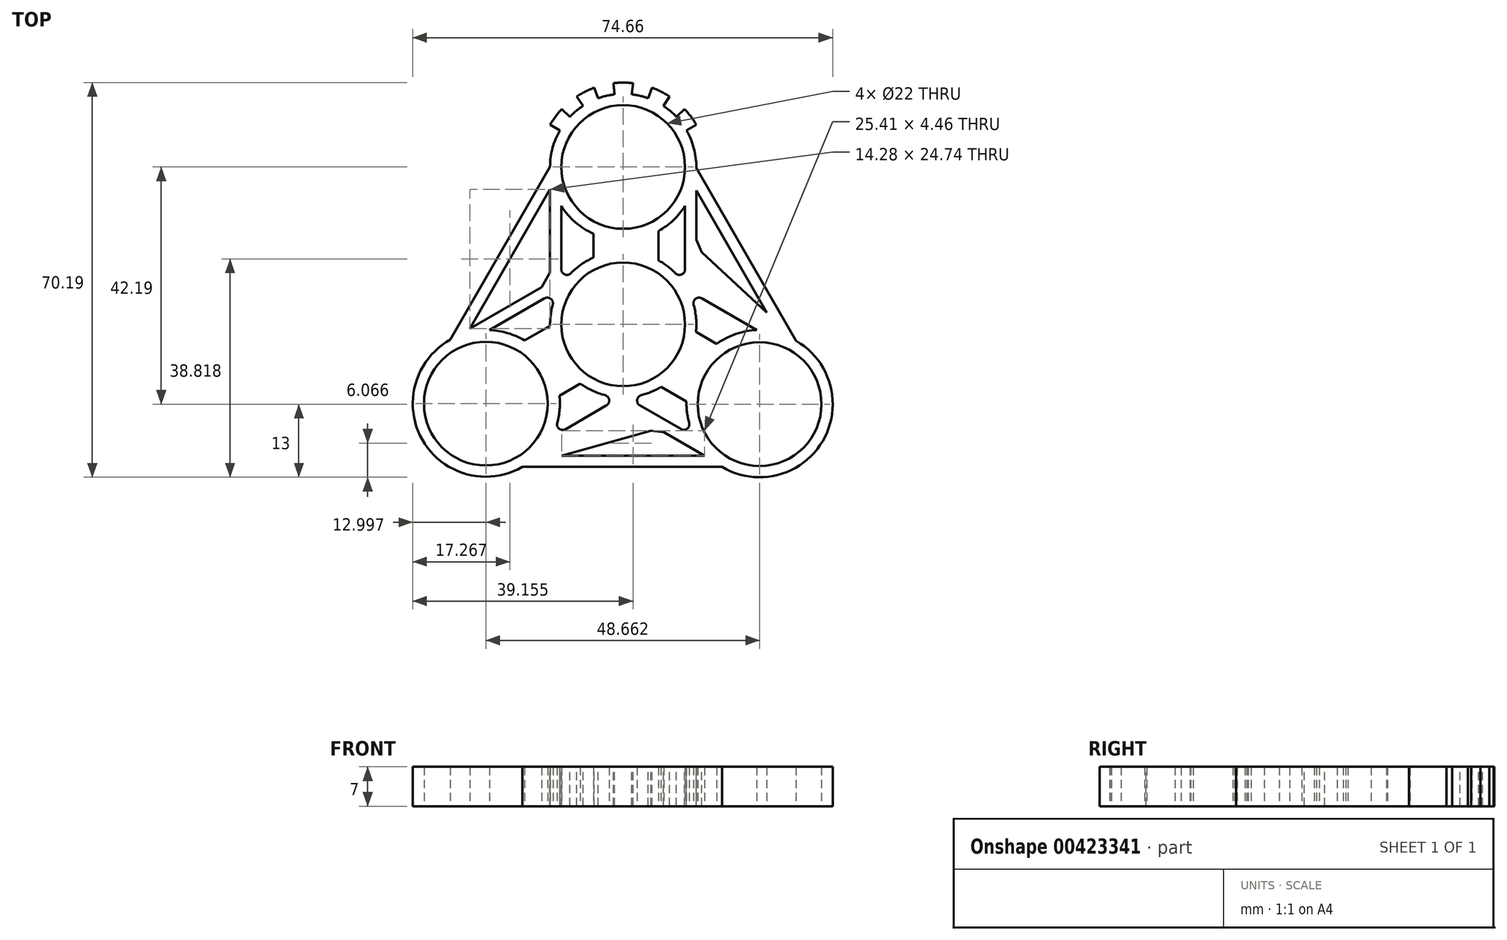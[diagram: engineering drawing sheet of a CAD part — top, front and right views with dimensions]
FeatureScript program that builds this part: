
annotation { "Feature Type Name" : "Feature", "Feature Type Description" : "" }
export const myFeature = defineFeature(function(context is Context, id is Id, definition is map)
    precondition{}
    {
        {
            var Q0;
            Q0=qCreatedBy(makeId("Top.planeOp"),FACE);
            var sketch = newSketch(context, id + "F0", { "sketchPlane" : qUnion([Q0])});
            skCircle(sketch, "E0", {"center": v(0, 0) * mm, "radius": 11 * mm});
            skCircle(sketch, "E1", {"center": v(0, 28) * mm, "radius": 11 * mm});
            skLineSegment(sketch, "E2", {"start": v(-11, 6.93) * mm, "end": v(-11, 21.07) * mm});
            skLineSegment(sketch, "E3", {"start": v(11, 21.07) * mm, "end": v(11, 6.93) * mm});
            skArc(sketch, "E4.0", {"start": v(-5.3, 11.87) * mm, "mid": v(-8.52, 9.82) * mm, "end": v(-11, 6.93) * mm});
            skArc(sketch, "E5.0", {"start": v(6.27, 16.61) * mm, "mid": v(8.92, 18.54) * mm, "end": v(11, 21.07) * mm});
            skLineSegment(sketch, "E6", {"start": v(-5.3, 11.87) * mm, "end": v(-5.3, 16.13) * mm});
            skLineSegment(sketch, "E7", {"start": v(6.27, 11.39) * mm, "end": v(6.27, 16.61) * mm});
            skPoint(sketch, "E8.orphan", {"position": v(-11, 0) * mm});
            skPoint(sketch, "E9.orphan", {"position": v(11, 0) * mm});
            skLineSegment(sketch, "E10.0", {"start": v(13, 23.81) * mm, "end": v(13, 13.72) * mm});
            skArc(sketch, "E11.trimOffspring", {"start": v(13, 27.81) * mm, "mid": v(0.1, 41) * mm, "end": v(-13, 28) * mm});
            skArc(sketch, "E12.trimOffspring", {"start": v(11, 6.93) * mm, "mid": v(8.92, 9.46) * mm, "end": v(6.27, 11.39) * mm});
            skArc(sketch, "E13.trimOffspring", {"start": v(-13, 0) * mm, "mid": v(-13, -0.13) * mm, "end": v(-13, -0.26) * mm});
            skArc(sketch, "E14.trimOffspring", {"start": v(-11, 21.07) * mm, "mid": v(-8.52, 18.18) * mm, "end": v(-5.3, 16.13) * mm});
            skArc(sketch, "E15.1.0", {"start": v(-30.75, -2.74) * mm, "mid": v(-35.72, -20.51) * mm, "end": v(-17.91, -25.35) * mm});
            skCircle(sketch, "E15.1.1", {"center": v(-24.41, -14.1) * mm, "radius": 11 * mm});
            skArc(sketch, "E15.2.0", {"start": v(17.59, -25.35) * mm, "mid": v(35.46, -20.77) * mm, "end": v(30.75, -2.93) * mm});
            skCircle(sketch, "E15.2.1", {"center": v(24.25, -14.19) * mm, "radius": 11 * mm});
            skPoint(sketch, "E15.center", {"position": v(-0.05, -0.1) * mm});
            skLineSegment(sketch, "E16.1.0", {"start": v(-27.29, -0.74) * mm, "end": v(-13, 7.5) * mm});
            skArc(sketch, "E16.1.1", {"start": v(-12.75, -20.06) * mm, "mid": v(-11.49, -16.47) * mm, "end": v(-11.32, -12.66) * mm});
            skLineSegment(sketch, "E16.1.2", {"start": v(-13, -0.26) * mm, "end": v(-17.52, -2.88) * mm});
            skArc(sketch, "E16.1.3", {"start": v(-11.5, 6.06) * mm, "mid": v(-12.65, 3) * mm, "end": v(-13, -0.26) * mm});
            skArc(sketch, "E16.1.5", {"start": v(-17.52, -2.88) * mm, "mid": v(-20.52, -1.55) * mm, "end": v(-23.75, -1) * mm});
            skLineSegment(sketch, "E16.1.6", {"start": v(-23.75, -1) * mm, "end": v(-11.5, 6.06) * mm});
            skLineSegment(sketch, "E16.2.0", {"start": v(14.45, -23.35) * mm, "end": v(6.14, -18.55) * mm});
            skArc(sketch, "E16.2.1", {"start": v(23.75, -1) * mm, "mid": v(20, -1.71) * mm, "end": v(16.62, -3.47) * mm});
            skLineSegment(sketch, "E16.2.2", {"start": v(6.73, -11.12) * mm, "end": v(11.25, -13.74) * mm});
            skArc(sketch, "E16.2.3", {"start": v(0.5, -13) * mm, "mid": v(3.73, -12.45) * mm, "end": v(6.73, -11.12) * mm});
            skLineSegment(sketch, "E16.2.4", {"start": v(13, 13.72) * mm, "end": v(25.54, 2.1) * mm});
            skArc(sketch, "E16.2.5", {"start": v(11.25, -13.74) * mm, "mid": v(11.6, -17) * mm, "end": v(12.75, -20.06) * mm});
            skLineSegment(sketch, "E16.2.6", {"start": v(12.75, -20.06) * mm, "end": v(0.5, -13) * mm});
            skLineSegment(sketch, "E17.1.0", {"start": v(-0.5, -13) * mm, "end": v(-12.75, -20.06) * mm});
            skLineSegment(sketch, "E17.1.1", {"start": v(-7.63, -10.53) * mm, "end": v(-11.32, -12.66) * mm});
            skArc(sketch, "E17.1.2", {"start": v(-7.63, -10.53) * mm, "mid": v(-4.25, -12.29) * mm, "end": v(-0.5, -13) * mm});
            skLineSegment(sketch, "E17.2.0", {"start": v(11.5, 6.06) * mm, "end": v(23.75, -1) * mm});
            skLineSegment(sketch, "E17.2.1", {"start": v(12.93, -1.34) * mm, "end": v(16.62, -3.47) * mm});
            skArc(sketch, "E17.2.2", {"start": v(12.93, -1.34) * mm, "mid": v(12.76, 2.47) * mm, "end": v(11.5, 6.06) * mm});
            skPoint(sketch, "E18.orphan", {"position": v(-6.66, 11.16) * mm});
            skLineSegment(sketch, "E19.trimOffspring", {"start": v(-13, 7.5) * mm, "end": v(-13, 24) * mm});
            skPoint(sketch, "E20.orphan", {"position": v(-6.34, -11.35) * mm});
            skLineSegment(sketch, "E21.trimOffspring", {"start": v(6.14, -18.55) * mm, "end": v(-10.96, -23.35) * mm});
            skArc(sketch, "E22.trimOffspring", {"start": v(12.93, -1.34) * mm, "mid": v(12.99, -0.58) * mm, "end": v(13, 0.19) * mm});
            skPoint(sketch, "E23.orphan", {"position": v(9.1, 17.33) * mm});
            skLineSegment(sketch, "E24", {"start": v(-30.75, -2.74) * mm, "end": v(-13, 28) * mm});
            skLineSegment(sketch, "E25", {"start": v(-17.91, -25.35) * mm, "end": v(17.59, -25.35) * mm});
            skLineSegment(sketch, "E26", {"start": v(13, 27.81) * mm, "end": v(30.75, -2.93) * mm});
            skLineSegment(sketch, "E27.0", {"start": v(-27.29, -0.74) * mm, "end": v(-13, 24) * mm});
            skLineSegment(sketch, "E28.0", {"start": v(13, 23.81) * mm, "end": v(25.54, 2.1) * mm});
            skLineSegment(sketch, "E29.0", {"start": v(-10.96, -23.35) * mm, "end": v(14.45, -23.35) * mm});
            skPoint(sketch, "E30.orphan", {"position": v(-30.58, -2.65) * mm});
            skPoint(sketch, "E31.orphan", {"position": v(30.75, -2.74) * mm});
            skPoint(sketch, "E32.orphan", {"position": v(17.59, -25.16) * mm});
            skPoint(sketch, "E33.orphan", {"position": v(-17.75, -25.26) * mm});
            skSolve(sketch);
        }
        {
            var Q0;
            Q0 = qSketchRegion(id + "F0", true);
            extrude(context, id + "F1", {"entities" : qUnion([Q0]), "depth" : 7 * mm});
        }
        {
            var Q0;
            Q0=makeQuery(id+"F1.opExtrude","SWEPT_EDGE",EDGE,{"disambiguationData":[OSD([sQuery(id+"F0.wireOp",EDGE,"E16.1.0"),sQuery(id+"F0.wireOp",EDGE,"E19.trimOffspring")])]});
            var Q1;
            Q1=makeQuery(id+"F1.opExtrude","SWEPT_EDGE",EDGE,{"disambiguationData":[OSD([sQuery(id+"F0.wireOp",EDGE,"E10.0"),sQuery(id+"F0.wireOp",EDGE,"E16.2.4")])]});
            var Q2;
            Q2=makeQuery(id+"F1.opExtrude","SWEPT_EDGE",EDGE,{"disambiguationData":[OSD([sQuery(id+"F0.wireOp",EDGE,"E16.2.0"),sQuery(id+"F0.wireOp",EDGE,"E21.trimOffspring")])]});
            chamfer(context, id + "F2", {"entities" : qUnion([Q0, Q1, Q2]), "width" : 3 * mm, "tangentPropagation" : true});
        }
        {
            var Q0;
            Q0=makeQuery(id+"F1.opExtrude","CAP_FACE",FACE,{"disambiguationData":[OSD([sQuery(id+"F0.wireOp",EDGE,"E0"),sQuery(id+"F0.wireOp",EDGE,"E1"),sQuery(id+"F0.wireOp",EDGE,"E2"),sQuery(id+"F0.wireOp",EDGE,"E3"),sQuery(id+"F0.wireOp",EDGE,"E4.0"),sQuery(id+"F0.wireOp",EDGE,"E5.0"),sQuery(id+"F0.wireOp",EDGE,"E6"),sQuery(id+"F0.wireOp",EDGE,"E7"),sQuery(id+"F0.wireOp",EDGE,"E10.0"),sQuery(id+"F0.wireOp",EDGE,"E11.trimOffspring"),sQuery(id+"F0.wireOp",EDGE,"E12.trimOffspring"),sQuery(id+"F0.wireOp",EDGE,"E14.trimOffspring"),sQuery(id+"F0.wireOp",EDGE,"E15.1.0"),sQuery(id+"F0.wireOp",EDGE,"E15.1.1"),sQuery(id+"F0.wireOp",EDGE,"E15.2.0"),sQuery(id+"F0.wireOp",EDGE,"E15.2.1"),sQuery(id+"F0.wireOp",EDGE,"E16.1.0"),sQuery(id+"F0.wireOp",EDGE,"E16.1.1"),sQuery(id+"F0.wireOp",EDGE,"E16.1.2"),sQuery(id+"F0.wireOp",EDGE,"E16.1.3"),sQuery(id+"F0.wireOp",EDGE,"E16.1.5"),sQuery(id+"F0.wireOp",EDGE,"E16.1.6"),sQuery(id+"F0.wireOp",EDGE,"E16.2.0"),sQuery(id+"F0.wireOp",EDGE,"E16.2.1"),sQuery(id+"F0.wireOp",EDGE,"E16.2.2"),sQuery(id+"F0.wireOp",EDGE,"E16.2.4"),sQuery(id+"F0.wireOp",EDGE,"E16.2.5"),sQuery(id+"F0.wireOp",EDGE,"E16.2.6"),sQuery(id+"F0.wireOp",EDGE,"E17.1.0"),sQuery(id+"F0.wireOp",EDGE,"E17.1.1"),sQuery(id+"F0.wireOp",EDGE,"E17.2.0"),sQuery(id+"F0.wireOp",EDGE,"E17.2.1"),sQuery(id+"F0.wireOp",EDGE,"E17.2.2"),sQuery(id+"F0.wireOp",EDGE,"E19.trimOffspring"),sQuery(id+"F0.wireOp",EDGE,"E17.1.2"),sQuery(id+"F0.wireOp",EDGE,"E21.trimOffspring"),sQuery(id+"F0.wireOp",EDGE,"E16.2.3"),sQuery(id+"F0.wireOp",EDGE,"E22.trimOffspring"),sQuery(id+"F0.wireOp",EDGE,"E24"),sQuery(id+"F0.wireOp",EDGE,"E25"),sQuery(id+"F0.wireOp",EDGE,"E26"),sQuery(id+"F0.wireOp",EDGE,"E27.0"),sQuery(id+"F0.wireOp",EDGE,"E28.0"),sQuery(id+"F0.wireOp",EDGE,"E29.0")])],"isStart":false});
            var sketch = newSketch(context, id + "F3", { "sketchPlane" : qUnion([Q0])});
            skArc(sketch, "E34.0", {"start": v(11.26, 34.5) * mm, "mid": v(10.43, 35.76) * mm, "end": v(9.46, 36.92) * mm});
            skArc(sketch, "E35.0", {"start": v(13, 35.5) * mm, "mid": v(12.03, 36.96) * mm, "end": v(10.91, 38.3) * mm});
            skLineSegment(sketch, "E36", {"start": v(0, 28) * mm, "end": v(0, 39) * mm, "construction": true});
            skLineSegment(sketch, "E37", {"start": v(-11.26, 34.5) * mm, "end": v(-13, 35.5) * mm});
            skLineSegment(sketch, "E38.1.0", {"start": v(-9.46, 36.92) * mm, "end": v(-10.91, 38.3) * mm});
            skLineSegment(sketch, "E38.2.0", {"start": v(-7.14, 38.86) * mm, "end": v(-8.24, 40.53) * mm});
            skLineSegment(sketch, "E38.anchor1", {"start": v(0, 28) * mm, "end": v(-13, 35.5) * mm, "construction": true});
            skLineSegment(sketch, "E38.anchor2", {"start": v(0, 28) * mm, "end": v(13, 35.5) * mm, "construction": true});
            skLineSegment(sketch, "E39.2.3.0", {"start": v(-4.45, 40.22) * mm, "end": v(-5.13, 42.1) * mm});
            skLineSegment(sketch, "E39.2.4.0", {"start": v(-1.5, 40.91) * mm, "end": v(-1.74, 42.9) * mm});
            skLineSegment(sketch, "E39.2.5.0", {"start": v(1.5, 40.91) * mm, "end": v(1.74, 42.9) * mm});
            skLineSegment(sketch, "E39.2.6.0", {"start": v(4.45, 40.22) * mm, "end": v(5.13, 42.1) * mm});
            skLineSegment(sketch, "E39.2.7.0", {"start": v(7.14, 38.86) * mm, "end": v(8.24, 40.53) * mm});
            skLineSegment(sketch, "E39.2.8.0", {"start": v(9.46, 36.92) * mm, "end": v(10.91, 38.3) * mm});
            skLineSegment(sketch, "E39.2.9.0", {"start": v(11.26, 34.5) * mm, "end": v(13, 35.5) * mm});
            skPoint(sketch, "E40.orphan", {"position": v(-13, 28) * mm});
            skArc(sketch, "E41.trimOffspring", {"start": v(-9.46, 36.92) * mm, "mid": v(-10.43, 35.76) * mm, "end": v(-11.26, 34.5) * mm});
            skArc(sketch, "E42.trimOffspring", {"start": v(-10.91, 38.3) * mm, "mid": v(-12.03, 36.96) * mm, "end": v(-13, 35.5) * mm});
            skArc(sketch, "E43.trimOffspring", {"start": v(-4.45, 40.22) * mm, "mid": v(-5.83, 39.62) * mm, "end": v(-7.14, 38.86) * mm});
            skArc(sketch, "E44.trimOffspring", {"start": v(-5.13, 42.1) * mm, "mid": v(-6.73, 41.4) * mm, "end": v(-8.24, 40.53) * mm});
            skArc(sketch, "E45.trimOffspring", {"start": v(1.5, 40.91) * mm, "mid": v(0, 41) * mm, "end": v(-1.5, 40.91) * mm});
            skArc(sketch, "E46.trimOffspring", {"start": v(1.74, 42.9) * mm, "mid": v(0, 43) * mm, "end": v(-1.74, 42.9) * mm});
            skArc(sketch, "E47.trimOffspring", {"start": v(8.24, 40.53) * mm, "mid": v(6.73, 41.4) * mm, "end": v(5.13, 42.1) * mm});
            skArc(sketch, "E48.trimOffspring", {"start": v(7.14, 38.86) * mm, "mid": v(5.83, 39.62) * mm, "end": v(4.45, 40.22) * mm});
            skPoint(sketch, "E49.orphan", {"position": v(13, 27.81) * mm});
            skSolve(sketch);
        }
        {
            var Q0;
            Q0 = qSketchRegion(id + "F3", true);
            extrude(context, id + "F4", {"entities" : qUnion([Q0]), "operationType" : NewBodyOperationType.ADD, "oppositeDirection" : true, "depth" : 7 * mm});
        }
        {
            var Q0;
            Q0=makeQuery(id+"F1.opExtrude","SWEPT_EDGE",EDGE,{"disambiguationData":[OSD([sQuery(id+"F0.wireOp",EDGE,"E16.1.3"),sQuery(id+"F0.wireOp",EDGE,"E16.1.6")])]});
            var Q1;
            Q1=makeQuery(id+"F1.opExtrude","SWEPT_EDGE",EDGE,{"disambiguationData":[OSD([sQuery(id+"F0.wireOp",EDGE,"E2"),sQuery(id+"F0.wireOp",EDGE,"E4.0")])]});
            var Q2;
            Q2=makeQuery(id+"F1.opExtrude","SWEPT_EDGE",EDGE,{"disambiguationData":[OSD([sQuery(id+"F0.wireOp",EDGE,"E3"),sQuery(id+"F0.wireOp",EDGE,"E12.trimOffspring")])]});
            var Q3;
            Q3=makeQuery(id+"F1.opExtrude","SWEPT_EDGE",EDGE,{"disambiguationData":[OSD([sQuery(id+"F0.wireOp",EDGE,"E17.2.0"),sQuery(id+"F0.wireOp",EDGE,"E17.2.2")])]});
            var Q4;
            Q4=makeQuery(id+"F1.opExtrude","SWEPT_EDGE",EDGE,{"disambiguationData":[OSD([sQuery(id+"F0.wireOp",EDGE,"E17.1.0"),sQuery(id+"F0.wireOp",EDGE,"E17.1.2")])]});
            var Q5;
            Q5=makeQuery(id+"F1.opExtrude","SWEPT_EDGE",EDGE,{"disambiguationData":[OSD([sQuery(id+"F0.wireOp",EDGE,"E16.2.6"),sQuery(id+"F0.wireOp",EDGE,"E16.2.3")])]});
            fillet(context, id + "F5", {"entities" : qUnion([Q0, Q1, Q2, Q3, Q4, Q5]), "radius" : 1 * mm, "tangentPropagation" : true, "allowEdgeOverflow" : false});
        }
    });
